# Revit family: TD92_ELO726_MAR050_RVT20_R00
name_source: partatom
category: Mobiliário
units: mm (PartAtom-declared; Revit-internal decimal feet)

## family parameters
Com base no plano de trabalho = Não
Compartilhado = Não
Corte com vazios quando carregada = Não
Número OmniClass = 23.40.20.00
Ponto de cálculo do ambiente = Não
Sempre na vertical = Sim
Título OmniClass = General Furniture and Specialties

## types (1)
- TD92_ELO726_MAR050_RVT20_R00
    Descrição = Integração e modularidade para compor amplos ambientes com magnitude e robustez. O Banco Tramontina Elo Central em Polietileno 3 Lugares é perfeito para compor ambientes de grandes proporções com magnitude e robustez, primando sempre pelo bom gosto e pelo design. Produto fabricado em polietileno em processo de rotomoldagem, segue tendências modernas, ambientando áreas coletivas (sejam elas internas ou externas) através da modularidade.
    Elevação padrão = 0  [stored 0 ft]
    Fabricante = Tramontina Delta S/A
    Modelo = Banco Tramontina Elo Central em Polietileno Marsala 3 Lugares
    Nota-chave = 92726050
    URL = https://www.tramontinastore.com

note: [stored X ft] marks values corroborated as IEEE doubles in the binary element streams (Revit-internal decimal feet)
